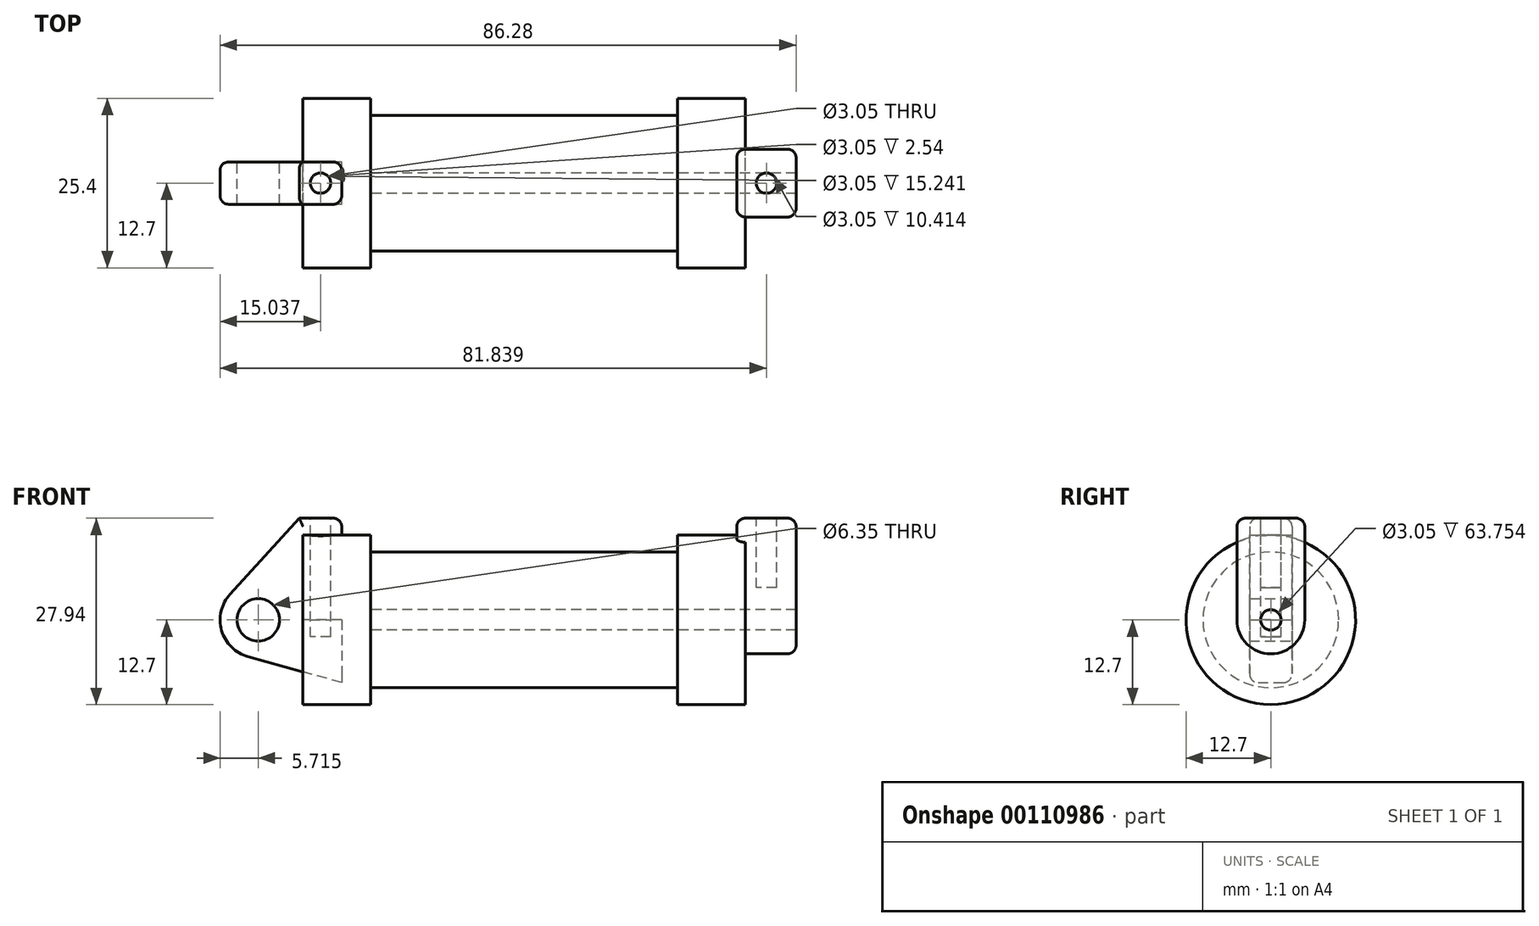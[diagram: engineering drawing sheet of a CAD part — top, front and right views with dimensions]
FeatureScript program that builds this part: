
annotation { "Feature Type Name" : "Feature", "Feature Type Description" : "" }
export const myFeature = defineFeature(function(context is Context, id is Id, definition is map)
    precondition{}
    {
        {
            var Q0;
            Q0=qCreatedBy(makeId("Front.planeOp"),FACE);
            var sketch = newSketch(context, id + "F0", { "sketchPlane" : qUnion([Q0])});
            skLineSegment(sketch, "E0", {"start": v(0, 0) * mm, "end": v(0, 12.7) * mm});
            skLineSegment(sketch, "E1", {"start": v(0, 12.7) * mm, "end": v(10.16, 12.7) * mm});
            skLineSegment(sketch, "E2", {"start": v(10.16, 12.7) * mm, "end": v(10.16, 10.16) * mm});
            skLineSegment(sketch, "E3", {"start": v(10.16, 10.16) * mm, "end": v(56.13, 10.16) * mm});
            skLineSegment(sketch, "E4", {"start": v(56.13, 10.16) * mm, "end": v(56.13, 12.7) * mm});
            skLineSegment(sketch, "E5", {"start": v(56.13, 12.7) * mm, "end": v(66.3, 12.7) * mm});
            skLineSegment(sketch, "E6", {"start": v(66.3, 12.7) * mm, "end": v(66.3, 0) * mm});
            skLineSegment(sketch, "E7", {"start": v(66.3, 0) * mm, "end": v(0, 0) * mm});
            skLineSegment(sketch, "E8", {"start": v(5.84, 15.24) * mm, "end": v(-0.5, 15.24) * mm});
            skLineSegment(sketch, "E9", {"start": v(-0.5, 15.24) * mm, "end": v(-10.88, 3.85) * mm});
            skLineSegment(sketch, "E10", {"start": v(0, 0) * mm, "end": v(-6.65, 0) * mm});
            skCircle(sketch, "E11", {"center": v(-6.65, 0) * mm, "radius": 5.72 * mm});
            skCircle(sketch, "E12", {"center": v(-6.65, 0) * mm, "radius": 3.18 * mm});
            skLineSegment(sketch, "E13", {"start": v(5.84, 15.24) * mm, "end": v(5.84, -9.4) * mm});
            skLineSegment(sketch, "E14", {"start": v(5.84, -9.4) * mm, "end": v(-8.18, -5.5) * mm});
            skSolve(sketch);
        }
        {
            var Q0;
            {var subQ0=sQuery(id+"F0.wireOp",EDGE,"E2");Q0=makeQuery(id+"F0.imprint","IMPRINT",FACE,{"disambiguationData":[TD([[makeQuery(id+"F0.imprint","IMPRINT",EDGE,{"derivedFrom":subQ0}),-1.0]])]});}
            var Q1;
            {var subQ0=sQuery(id+"F0.wireOp",EDGE,"E0");Q1=makeQuery(id+"F0.imprint","IMPRINT",FACE,{"disambiguationData":[TD([[makeQuery(id+"F0.imprint","IMPRINT",EDGE,{"derivedFrom":subQ0}),-1.0]])]});}
            var Q2;
            Q2=sQuery(id+"F0.wireOp",EDGE,"E7");
            revolve(context, id + "F1", {"entities" : qUnion([Q0, Q1]), "axis" : qUnion([Q2]), "revolveType" : RevolveType.FULL});
        }
        {
            var Q0;
            {var subQ3=sQuery(id+"F0.wireOp",EDGE,"E0");Q0=makeQuery(id+"F0.imprint","IMPRINT",FACE,{"disambiguationData":[TD([[makeQuery(id+"F0.imprint","IMPRINT",EDGE,{"derivedFrom":subQ3}),1.0]])]});}
            var Q1;
            {var subQ0=sQuery(id+"F0.wireOp",EDGE,"E14");Q1=makeQuery(id+"F0.imprint","IMPRINT",FACE,{"disambiguationData":[TD([[makeQuery(id+"F0.imprint","IMPRINT",EDGE,{"derivedFrom":subQ0}),-1.0]])]});}
            var Q2;
            {var subQ4=sQuery(id+"F0.wireOp",EDGE,"E12");Q2=makeQuery(id+"F0.imprint","IMPRINT",FACE,{"disambiguationData":[TD([[makeQuery(id+"F0.imprint","IMPRINT",EDGE,{"derivedFrom":subQ4}),-1.0]])]});}
            extrude(context, id + "F2", {"entities" : qUnion([Q0, Q1, Q2]), "endBound" : BoundingType.SYMMETRIC, "depth" : 6.35 * mm});
        }
        {
            var Q0;
            Q0=makeQuery(id+"F1.opRevolve","SWEPT_FACE",FACE,{"disambiguationData":[OSD([sQuery(id+"F0.wireOp",EDGE,"E6")])]});
            var sketch = newSketch(context, id + "F3", { "sketchPlane" : qUnion([Q0])});
            skCircle(sketch, "E15", {"center": v(0, 0) * mm, "radius": 5.08 * mm});
            skCircle(sketch, "E16", {"center": v(0, 0) * mm, "radius": 1.52 * mm});
            skLineSegment(sketch, "E17", {"start": v(-5.08, 0) * mm, "end": v(-5.08, 15.24) * mm});
            skLineSegment(sketch, "E18", {"start": v(5.08, 0) * mm, "end": v(5.08, 15.24) * mm});
            skLineSegment(sketch, "E19", {"start": v(-5.08, 15.24) * mm, "end": v(5.08, 15.24) * mm});
            skSolve(sketch);
        }
        {
            var Q0;
            {var subQ0=sQuery(id+"F3.wireOp",EDGE,"E19");Q0=makeQuery(id+"F3.imprint","IMPRINT",FACE,{"disambiguationData":[TD([[makeQuery(id+"F3.imprint","IMPRINT",EDGE,{"derivedFrom":subQ0}),-1.0]])]});}
            var Q1;
            {var subQ0=sQuery(id+"F3.wireOp",EDGE,"E17");var subQ1=sQuery(id+"F3.wireOp",EDGE,"E15");var subQ2=makeQuery(id+"F3.imprint","INTERSECT",VERTEX,{"derivedFrom":[subQ1,subQ0]});Q1=makeQuery(id+"F3.imprint","IMPRINT",FACE,{"disambiguationData":[TD([[makeQuery(id+"F3.imprint","IMPRINT",EDGE,{"disambiguationData":[TD([[subQ2,1.0]])],"derivedFrom":subQ1}),-1.0]])]});}
            var Q2;
            Q2=makeQuery(id+"F3.imprint","IMPRINT",FACE,{"disambiguationData":[TD([[makeQuery(id+"F3.imprint","IMPRINT",EDGE,{"derivedFrom":sQuery(id+"F3.wireOp",EDGE,"E16")}),-1.0]])]});
            extrude(context, id + "F4", {"entities" : qUnion([Q0, Q1, Q2]), "operationType" : NewBodyOperationType.ADD, "depth" : 7.62 * mm});
        }
        {
            var Q0;
            Q0=makeQuery(id+"F4.opExtrude","CAP_FACE",FACE,{"disambiguationData":[OSD([sQuery(id+"F3.wireOp",EDGE,"E15"),sQuery(id+"F3.wireOp",EDGE,"E16"),sQuery(id+"F3.wireOp",EDGE,"E17"),sQuery(id+"F3.wireOp",EDGE,"E18"),sQuery(id+"F3.wireOp",EDGE,"E19")])],"isStart":true});
            extrude(context, id + "F5", {"entities" : qUnion([Q0]), "operationType" : NewBodyOperationType.ADD, "depth" : 1.27 * mm});
        }
        {
            var Q0;
            Q0=makeQuery(id+"F4.boolean.opBoolean","SPLIT",FACE,{"disambiguationData":[TD([makeQuery(id+"F4.opExtrude","SWEPT_FACE",FACE,{"disambiguationData":[OSD([sQuery(id+"F3.wireOp",EDGE,"E16")])]})])],"derivedFrom":makeQuery(id+"F1.opRevolve","SWEPT_FACE",FACE,{"disambiguationData":[OSD([sQuery(id+"F0.wireOp",EDGE,"E6")])]})});
            var Q1;
            Q1=makeQuery(id+"F1.opRevolve","SWEPT_FACE",FACE,{"disambiguationData":[OSD([sQuery(id+"F0.wireOp",EDGE,"E2")])]});
            extrude(context, id + "F6", {"entities" : qUnion([Q0]), "operationType" : NewBodyOperationType.REMOVE, "endBound" : BoundingType.UP_TO_SURFACE, "oppositeDirection" : true, "endBoundEntityFace" : qUnion([Q1]), "depth" : 25.4 * mm});
        }
        {
            var Q0;
            {var subQ0=sQuery(id+"F3.wireOp",EDGE,"E19");Q0=makeQuery(id+"F5.boolean.opBoolean","MERGE",FACE,{"derivedFrom":[makeQuery(id+"F4.opExtrude","SWEPT_FACE",FACE,{"disambiguationData":[OSD([subQ0])]}),makeQuery(id+"F5.opExtrude","SWEPT_FACE",FACE,{"disambiguationData":[OSD([subQ0])]})]});}
            var sketch = newSketch(context, id + "F7", { "sketchPlane" : qUnion([Q0])});
            skCircle(sketch, "E20", {"center": v(69.47, 0) * mm, "radius": 1.52 * mm});
            skPoint(sketch, "E20.centerSnap0", {"position": v(69.47, -5.08) * mm});
            skPoint(sketch, "E20.centerSnap1", {"position": v(73.91, 0) * mm});
            skSolve(sketch);
        }
        {
            var Q0;
            Q0=makeQuery(id+"F2.opExtrude","SWEPT_FACE",FACE,{"disambiguationData":[OSD([sQuery(id+"F0.wireOp",EDGE,"E8")])]});
            var sketch = newSketch(context, id + "F8", { "sketchPlane" : qUnion([Q0])});
            skCircle(sketch, "E21", {"center": v(2.67, 0) * mm, "radius": 1.52 * mm});
            skPoint(sketch, "E21.centerSnap0", {"position": v(2.67, -3.18) * mm});
            skPoint(sketch, "E21.centerSnap1", {"position": v(-0.5, 0) * mm});
            skSolve(sketch);
        }
        {
            var Q0;
            Q0 = qSketchRegion(id + "F8", true);
            extrude(context, id + "F9", {"entities" : qUnion([Q0]), "operationType" : NewBodyOperationType.REMOVE, "oppositeDirection" : true, "depth" : 17.78 * mm});
        }
        {
            var Q0;
            Q0=makeQuery(id+"F4.opExtrude","CAP_EDGE",EDGE,{"disambiguationData":[OSD([sQuery(id+"F3.wireOp",EDGE,"E17")])],"isStart":false});
            var Q1;
            {var subQ0=sQuery(id+"F3.wireOp",EDGE,"E19");var subQ1=sQuery(id+"F3.wireOp",EDGE,"E17");Q1=makeQuery(id+"F5.boolean.opBoolean","MERGE",EDGE,{"derivedFrom":[makeQuery(id+"F4.opExtrude","SWEPT_EDGE",EDGE,{"disambiguationData":[OSD([subQ1,subQ0])]}),makeQuery(id+"F5.opExtrude","SWEPT_EDGE",EDGE,{"disambiguationData":[OSD([subQ1,subQ0])]})]});}
            var Q2;
            {var subQ0=sQuery(id+"F3.wireOp",EDGE,"E19");var subQ1=sQuery(id+"F3.wireOp",EDGE,"E18");Q2=makeQuery(id+"F5.boolean.opBoolean","MERGE",EDGE,{"derivedFrom":[makeQuery(id+"F4.opExtrude","SWEPT_EDGE",EDGE,{"disambiguationData":[OSD([subQ1,subQ0])]}),makeQuery(id+"F5.opExtrude","SWEPT_EDGE",EDGE,{"disambiguationData":[OSD([subQ1,subQ0])]})]});}
            var Q3;
            Q3=makeQuery(id+"F4.opExtrude","CAP_EDGE",EDGE,{"disambiguationData":[OSD([sQuery(id+"F3.wireOp",EDGE,"E19")])],"isStart":false});
            var Q4;
            Q4=makeQuery(id+"F5.opExtrude","CAP_EDGE",EDGE,{"disambiguationData":[OSD([sQuery(id+"F3.wireOp",EDGE,"E19")])],"isStart":false});
            var Q5;
            Q5=makeQuery(id+"F2.opExtrude","CAP_EDGE",EDGE,{"disambiguationData":[OSD([sQuery(id+"F0.wireOp",EDGE,"E9")])],"isStart":true});
            var Q6;
            Q6=makeQuery(id+"F2.opExtrude","CAP_EDGE",EDGE,{"disambiguationData":[OSD([sQuery(id+"F0.wireOp",EDGE,"E9")])],"isStart":false});
            var Q7;
            Q7=makeQuery(id+"F2.opExtrude","CAP_EDGE",EDGE,{"disambiguationData":[OSD([sQuery(id+"F0.wireOp",EDGE,"E8")])],"isStart":true});
            var Q8;
            Q8=makeQuery(id+"F2.opExtrude","CAP_EDGE",EDGE,{"disambiguationData":[OSD([sQuery(id+"F0.wireOp",EDGE,"E8")])],"isStart":false});
            var Q9;
            Q9=makeQuery(id+"F2.opExtrude","SWEPT_EDGE",EDGE,{"disambiguationData":[OSD([sQuery(id+"F0.wireOp",EDGE,"E8"),sQuery(id+"F0.wireOp",EDGE,"E13")])]});
            var Q10;
            Q10=makeQuery(id+"F5.opExtrude","CAP_EDGE",EDGE,{"disambiguationData":[OSD([sQuery(id+"F3.wireOp",EDGE,"E17")])],"isStart":false});
            var Q11;
            Q11=makeQuery(id+"F5.opExtrude","CAP_EDGE",EDGE,{"disambiguationData":[OSD([sQuery(id+"F3.wireOp",EDGE,"E18")])],"isStart":false});
            var Q12;
            {var subQ0=sQuery(id+"F0.wireOp",EDGE,"E13");Q12=makeQuery(id+"F2.opExtrude","CAP_EDGE",EDGE,{"disambiguationData":[OSD([subQ0]),TDD([makeQuery(id+"F0.imprint","IMPRINT",EDGE,{"disambiguationData":[TD([[makeQuery(id+"F0.imprint","INTERSECT",VERTEX,{"derivedFrom":[sQuery(id+"F0.wireOp",EDGE,"E8"),subQ0]}),-1.0]])],"derivedFrom":subQ0})])],"isStart":true});}
            var Q13;
            {var subQ0=sQuery(id+"F0.wireOp",EDGE,"E13");Q13=makeQuery(id+"F2.opExtrude","CAP_EDGE",EDGE,{"disambiguationData":[OSD([subQ0]),TDD([makeQuery(id+"F0.imprint","IMPRINT",EDGE,{"disambiguationData":[TD([[makeQuery(id+"F0.imprint","INTERSECT",VERTEX,{"derivedFrom":[sQuery(id+"F0.wireOp",EDGE,"E8"),subQ0]}),-1.0]])],"derivedFrom":subQ0})])],"isStart":false});}
            fillet(context, id + "F10", {"entities" : qUnion([Q0, Q1, Q2, Q3, Q4, Q5, Q6, Q7, Q8, Q9, Q10, Q11, Q12, Q13]), "radius" : 1.27 * mm, "tangentPropagation" : true, "allowEdgeOverflow" : false});
        }
        {
            var Q0;
            Q0 = qSketchRegion(id + "F7", true);
            extrude(context, id + "F11", {"entities" : qUnion([Q0]), "operationType" : NewBodyOperationType.REMOVE, "oppositeDirection" : true, "depth" : 10.4 * mm});
        }
    });
